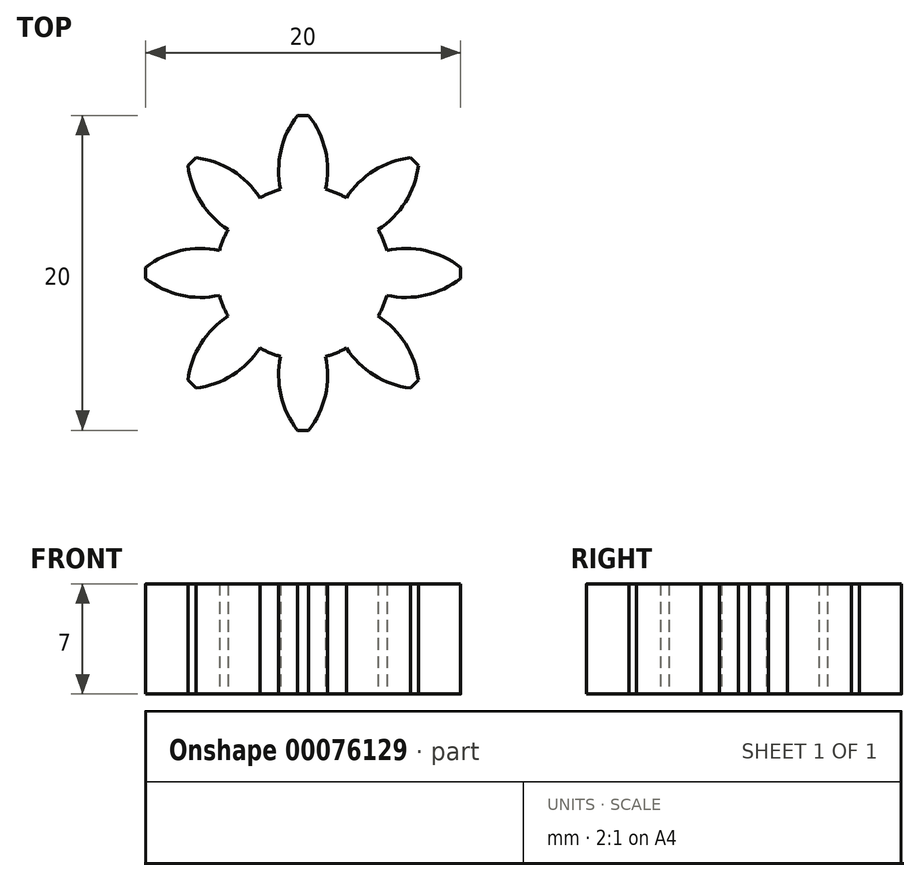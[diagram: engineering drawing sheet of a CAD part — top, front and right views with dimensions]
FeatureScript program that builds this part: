
annotation { "Feature Type Name" : "Feature", "Feature Type Description" : "" }
export const myFeature = defineFeature(function(context is Context, id is Id, definition is map)
    precondition{}
    {
        {
            var Q0;
            Q0=qCreatedBy(makeId("Top.planeOp"),FACE);
            var sketch = newSketch(context, id + "F0", { "sketchPlane" : qUnion([Q0])});
            skCircle(sketch, "E0", {"center": v(0, 0) * mm, "radius": 5.5 * mm});
            skCircle(sketch, "E1", {"center": v(0, 0) * mm, "radius": 8 * mm, "construction": true});
            skLineSegment(sketch, "E2", {"start": v(0, 0) * mm, "end": v(0, 10) * mm, "construction": true});
            skLineSegment(sketch, "E3", {"start": v(0, 0) * mm, "end": v(1.74, 9.85) * mm, "construction": true});
            skLineSegment(sketch, "E4", {"start": v(0, 8) * mm, "end": v(-32.72, 8) * mm, "construction": true});
            skLineSegment(sketch, "E5", {"start": v(0, 8) * mm, "end": v(-31.45, -3.45) * mm, "construction": true});
            skCircle(sketch, "E6", {"center": v(1.39, 7.88) * mm, "radius": 5.62 * mm, "construction": true});
            skArc(sketch, "E7", {"start": v(-2.52, 11.93) * mm, "mid": v(-8.9, 3.64) * mm, "end": v(1.42, 5.31) * mm, "construction": true});
            skArc(sketch, "E8", {"start": v(1.42, 5.31) * mm, "mid": v(1.56, 6.6) * mm, "end": v(1.39, 7.88) * mm});
            skArc(sketch, "E9", {"start": v(0.35, 10) * mm, "mid": v(-0.93, 11.19) * mm, "end": v(-2.52, 11.93) * mm, "construction": true});
            skArc(sketch, "E10", {"start": v(1.39, 7.88) * mm, "mid": v(0.98, 9) * mm, "end": v(0.35, 10) * mm});
            skArc(sketch, "E11", {"start": v(0, 10) * mm, "mid": v(-0.18, 10) * mm, "end": v(-0.35, 10) * mm});
            skArc(sketch, "E12", {"start": v(0.35, 10) * mm, "mid": v(0.18, 10) * mm, "end": v(0, 10) * mm});
            skArc(sketch, "E13.MirrorCS", {"start": v(-0.35, 10) * mm, "mid": v(-0.18, 10) * mm, "end": v(0, 10) * mm, "construction": true});
            skArc(sketch, "E14.MirrorCS", {"start": v(-1.39, 7.88) * mm, "mid": v(-0.99, 8.98) * mm, "end": v(-0.36, 9.98) * mm});
            skArc(sketch, "E15.MirrorCS", {"start": v(-1.42, 5.31) * mm, "mid": v(-1.56, 6.6) * mm, "end": v(-1.39, 7.88) * mm});
            skArc(sketch, "E16", {"start": v(-0.36, 9.98) * mm, "mid": v(-0.36, 9.99) * mm, "end": v(-0.35, 10) * mm});
            skArc(sketch, "E17", {"start": v(0, 10) * mm, "mid": v(0, 10) * mm, "end": v(0, 10) * mm, "construction": true});
            skArc(sketch, "E18", {"start": v(-0.36, 10) * mm, "mid": v(0, -10) * mm, "end": v(0.35, 10) * mm, "construction": true});
            skLineSegment(sketch, "E19", {"start": v(0, 10) * mm, "end": v(0, 10) * mm});
            skArc(sketch, "E20", {"start": v(-0.35, 10) * mm, "mid": v(-0.36, 10) * mm, "end": v(-0.36, 10) * mm, "construction": true});
            skSolve(sketch);
        }
        {
            var Q0;
            Q0 = qSketchRegion(id + "F0", true);
            extrude(context, id + "F1", {"entities" : qUnion([Q0]), "depth" : 7 * mm});
        }
        {
            var Q0;
            Q0=qCreatedBy(makeId("Right.planeOp"),FACE);
            var sketch = newSketch(context, id + "F2", { "sketchPlane" : qUnion([Q0])});
            skLineSegment(sketch, "E21", {"start": v(0, 43.93) * mm, "end": v(0, 0) * mm, "construction": true});
            skSolve(sketch);
        }
        {
            var Q0;
            Q0=makeQuery(id+"F1.opExtrude","SWEPT_BODY",BODY,{"disambiguationData":[OSD([sQuery(id+"F0.wireOp",EDGE,"E0"),sQuery(id+"F0.wireOp",EDGE,"E8"),sQuery(id+"F0.wireOp",EDGE,"E10"),sQuery(id+"F0.wireOp",EDGE,"E12"),sQuery(id+"F0.wireOp",EDGE,"E13.MirrorCS"),sQuery(id+"F0.wireOp",EDGE,"E14.MirrorCS"),sQuery(id+"F0.wireOp",EDGE,"E15.MirrorCS")])]});
            var Q1;
            Q1=sQuery(id+"F2.wireOp",EDGE,"E21");
            circularPattern(context, id + "F3", {"entities" : qUnion([Q0]), "axis" : qUnion([Q1]), "angle" : 45 * degree, "instanceCount" : 8, "computeTransformsWithoutBuiltin" : true});
        }
        {
            var Q0;
            Q0=makeQuery(id+"F3.opPattern","COPY",BODY,{"derivedFrom":makeQuery(id+"F1.opExtrude","SWEPT_BODY",BODY,{"disambiguationData":[OSD([sQuery(id+"F0.wireOp",EDGE,"E0"),sQuery(id+"F0.wireOp",EDGE,"E8"),sQuery(id+"F0.wireOp",EDGE,"E10"),sQuery(id+"F0.wireOp",EDGE,"E11"),sQuery(id+"F0.wireOp",EDGE,"E12"),sQuery(id+"F0.wireOp",EDGE,"E14.MirrorCS"),sQuery(id+"F0.wireOp",EDGE,"E15.MirrorCS"),sQuery(id+"F0.wireOp",EDGE,"E16")])]}),"instanceName":"6"});
            var Q1;
            Q1=makeQuery(id+"F3.opPattern","COPY",BODY,{"derivedFrom":makeQuery(id+"F1.opExtrude","SWEPT_BODY",BODY,{"disambiguationData":[OSD([sQuery(id+"F0.wireOp",EDGE,"E0"),sQuery(id+"F0.wireOp",EDGE,"E8"),sQuery(id+"F0.wireOp",EDGE,"E10"),sQuery(id+"F0.wireOp",EDGE,"E11"),sQuery(id+"F0.wireOp",EDGE,"E12"),sQuery(id+"F0.wireOp",EDGE,"E14.MirrorCS"),sQuery(id+"F0.wireOp",EDGE,"E15.MirrorCS"),sQuery(id+"F0.wireOp",EDGE,"E16")])]}),"instanceName":"5"});
            var Q2;
            Q2=makeQuery(id+"F3.opPattern","COPY",BODY,{"derivedFrom":makeQuery(id+"F1.opExtrude","SWEPT_BODY",BODY,{"disambiguationData":[OSD([sQuery(id+"F0.wireOp",EDGE,"E0"),sQuery(id+"F0.wireOp",EDGE,"E8"),sQuery(id+"F0.wireOp",EDGE,"E10"),sQuery(id+"F0.wireOp",EDGE,"E11"),sQuery(id+"F0.wireOp",EDGE,"E12"),sQuery(id+"F0.wireOp",EDGE,"E14.MirrorCS"),sQuery(id+"F0.wireOp",EDGE,"E15.MirrorCS"),sQuery(id+"F0.wireOp",EDGE,"E16")])]}),"instanceName":"4"});
            var Q3;
            Q3=makeQuery(id+"F3.opPattern","COPY",BODY,{"derivedFrom":makeQuery(id+"F1.opExtrude","SWEPT_BODY",BODY,{"disambiguationData":[OSD([sQuery(id+"F0.wireOp",EDGE,"E0"),sQuery(id+"F0.wireOp",EDGE,"E8"),sQuery(id+"F0.wireOp",EDGE,"E10"),sQuery(id+"F0.wireOp",EDGE,"E11"),sQuery(id+"F0.wireOp",EDGE,"E12"),sQuery(id+"F0.wireOp",EDGE,"E14.MirrorCS"),sQuery(id+"F0.wireOp",EDGE,"E15.MirrorCS"),sQuery(id+"F0.wireOp",EDGE,"E16")])]}),"instanceName":"3"});
            var Q4;
            Q4=makeQuery(id+"F3.opPattern","COPY",BODY,{"derivedFrom":makeQuery(id+"F1.opExtrude","SWEPT_BODY",BODY,{"disambiguationData":[OSD([sQuery(id+"F0.wireOp",EDGE,"E0"),sQuery(id+"F0.wireOp",EDGE,"E8"),sQuery(id+"F0.wireOp",EDGE,"E10"),sQuery(id+"F0.wireOp",EDGE,"E11"),sQuery(id+"F0.wireOp",EDGE,"E12"),sQuery(id+"F0.wireOp",EDGE,"E14.MirrorCS"),sQuery(id+"F0.wireOp",EDGE,"E15.MirrorCS"),sQuery(id+"F0.wireOp",EDGE,"E16")])]}),"instanceName":"2"});
            var Q5;
            Q5=makeQuery(id+"F3.opPattern","COPY",BODY,{"derivedFrom":makeQuery(id+"F1.opExtrude","SWEPT_BODY",BODY,{"disambiguationData":[OSD([sQuery(id+"F0.wireOp",EDGE,"E0"),sQuery(id+"F0.wireOp",EDGE,"E8"),sQuery(id+"F0.wireOp",EDGE,"E10"),sQuery(id+"F0.wireOp",EDGE,"E11"),sQuery(id+"F0.wireOp",EDGE,"E12"),sQuery(id+"F0.wireOp",EDGE,"E14.MirrorCS"),sQuery(id+"F0.wireOp",EDGE,"E15.MirrorCS"),sQuery(id+"F0.wireOp",EDGE,"E16")])]}),"instanceName":"1"});
            var Q6;
            Q6=makeQuery(id+"F1.opExtrude","SWEPT_BODY",BODY,{"disambiguationData":[OSD([sQuery(id+"F0.wireOp",EDGE,"E0"),sQuery(id+"F0.wireOp",EDGE,"E8"),sQuery(id+"F0.wireOp",EDGE,"E10"),sQuery(id+"F0.wireOp",EDGE,"E11"),sQuery(id+"F0.wireOp",EDGE,"E12"),sQuery(id+"F0.wireOp",EDGE,"E14.MirrorCS"),sQuery(id+"F0.wireOp",EDGE,"E15.MirrorCS"),sQuery(id+"F0.wireOp",EDGE,"E16")])]});
            var Q7;
            Q7=makeQuery(id+"F3.opPattern","COPY",BODY,{"derivedFrom":makeQuery(id+"F1.opExtrude","SWEPT_BODY",BODY,{"disambiguationData":[OSD([sQuery(id+"F0.wireOp",EDGE,"E0"),sQuery(id+"F0.wireOp",EDGE,"E8"),sQuery(id+"F0.wireOp",EDGE,"E10"),sQuery(id+"F0.wireOp",EDGE,"E11"),sQuery(id+"F0.wireOp",EDGE,"E12"),sQuery(id+"F0.wireOp",EDGE,"E14.MirrorCS"),sQuery(id+"F0.wireOp",EDGE,"E15.MirrorCS"),sQuery(id+"F0.wireOp",EDGE,"E16")])]}),"instanceName":"7"});
            booleanBodies(context, id + "F4", {"operationType" : BooleanOperationType.UNION, "tools" : qUnion([Q0, Q1, Q2, Q3, Q4, Q5, Q6, Q7])});
        }
    });
